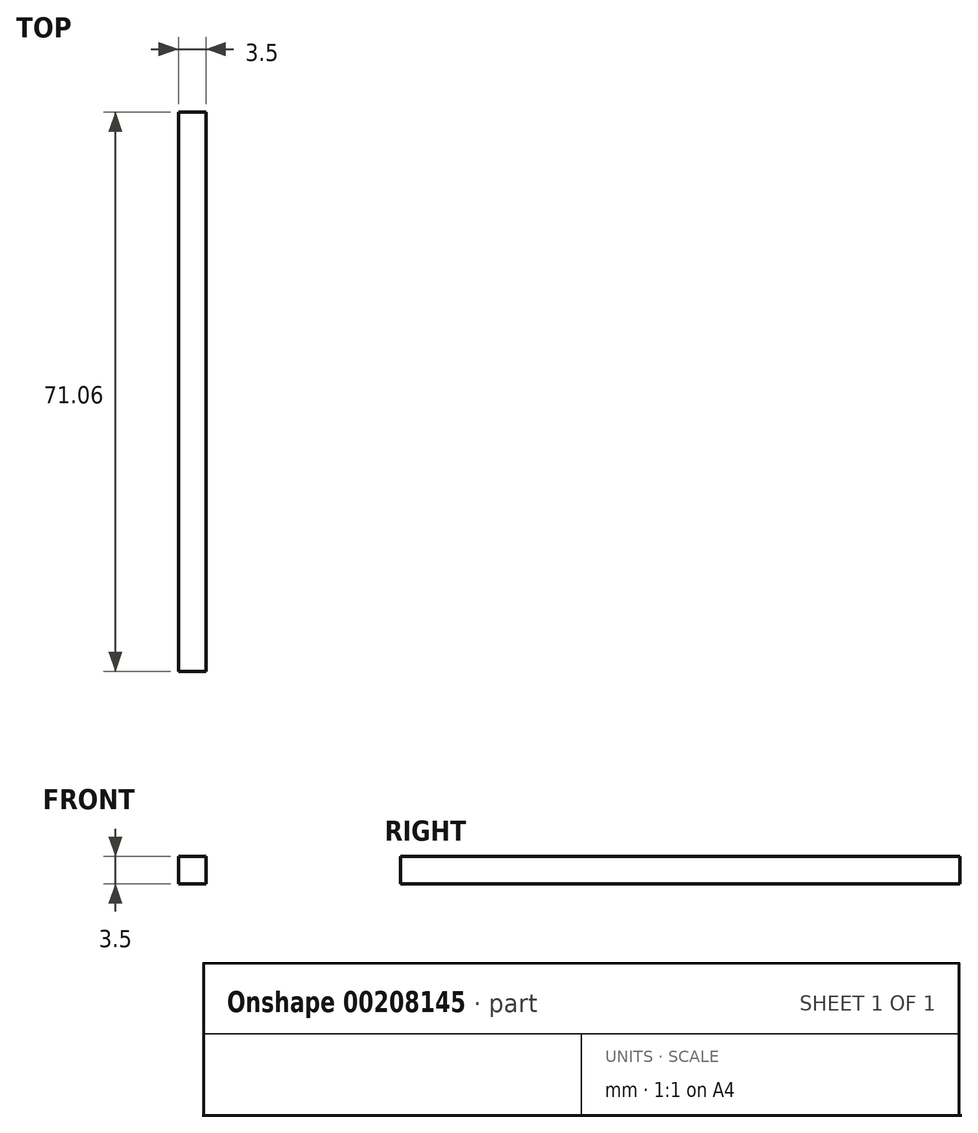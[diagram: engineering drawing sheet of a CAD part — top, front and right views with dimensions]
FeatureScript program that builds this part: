
annotation { "Feature Type Name" : "Feature", "Feature Type Description" : "" }
export const myFeature = defineFeature(function(context is Context, id is Id, definition is map)
    precondition{}
    {
        {
            var Q0;
            Q0=qCreatedBy(makeId("Top.planeOp"),FACE);
            var sketch = newSketch(context, id + "F0", { "sketchPlane" : qUnion([Q0])});
            skLineSegment(sketch, "E0.bottom", {"start": v(1.75, -35.53) * mm, "end": v(-1.75, -35.53) * mm});
            skLineSegment(sketch, "E0.top", {"start": v(1.75, 35.53) * mm, "end": v(-1.75, 35.53) * mm});
            skLineSegment(sketch, "E0.left", {"start": v(1.75, -35.53) * mm, "end": v(1.75, 35.53) * mm});
            skLineSegment(sketch, "E0.right", {"start": v(-1.75, -35.53) * mm, "end": v(-1.75, 35.53) * mm});
            skPoint(sketch, "E0.middle", {"position": v(0, 0) * mm});
            skSolve(sketch);
        }
        {
            var Q0;
            Q0 = qSketchRegion(id + "F0", true);
            extrude(context, id + "F1", {"entities" : qUnion([Q0]), "depth" : 3.5 * mm});
        }
    });
